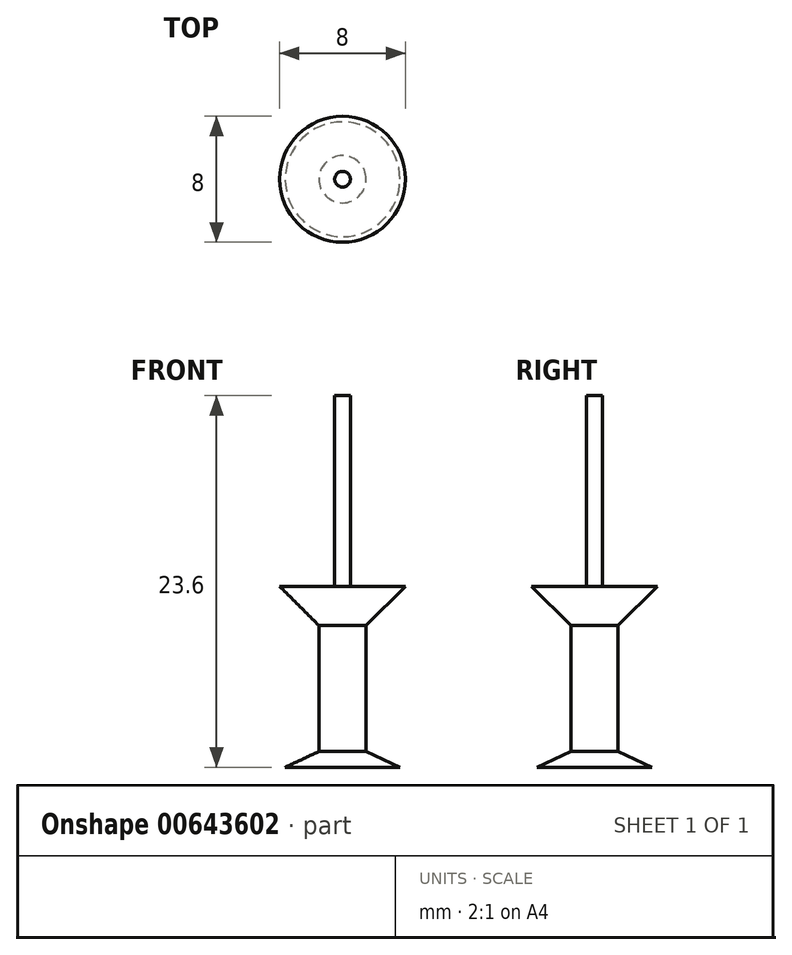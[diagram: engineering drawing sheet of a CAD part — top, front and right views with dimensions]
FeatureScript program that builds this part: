
annotation { "Feature Type Name" : "Feature", "Feature Type Description" : "" }
export const myFeature = defineFeature(function(context is Context, id is Id, definition is map)
    precondition{}
    {
        {
            var Q0;
            Q0=qCreatedBy(makeId("Right.planeOp"),FACE);
            var sketch = newSketch(context, id + "F0", { "sketchPlane" : qUnion([Q0])});
            skLineSegment(sketch, "E0", {"start": v(0, 0) * mm, "end": v(0.5, 0) * mm});
            skLineSegment(sketch, "E1", {"start": v(0.5, 0) * mm, "end": v(0, 0.87) * mm});
            skLineSegment(sketch, "E2", {"start": v(0, 0.87) * mm, "end": v(0, 0) * mm});
            skSolve(sketch);
        }
        {
            var Q0;
            Q0 = qSketchRegion(id + "F0", true);
            var Q1;
            Q1=sQuery(id+"F0.wireOp",EDGE,"E1");
            var Q2;
            Q2=sQuery(id+"F0.wireOp",EDGE,"E0");
            var Q3;
            Q3=sQuery(id+"F0.wireOp",EDGE,"E2");
            revolve(context, id + "F1", {"bodyType" : ToolBodyType.SURFACE, "entities" : qUnion([Q0]), "surfaceEntities" : qUnion([Q1, Q2]), "axis" : qUnion([Q3]), "revolveType" : RevolveType.FULL});
        }
        {
            var Q0;
            Q0=makeQuery(id+"F1.opRevolve","SWEPT_FACE",FACE,{"disambiguationData":[OSD([sQuery(id+"F0.wireOp",EDGE,"E0")])]});
            var sketch = newSketch(context, id + "F2", { "sketchPlane" : qUnion([Q0])});
            skSolve(sketch);
        }
        {
            var Q0;
            Q0=makeQuery(id+"F2.imprint","IMPRINT",FACE,{"disambiguationData":[TD([[makeQuery(id+"F2.imprint","IMPRINT",EDGE,{"derivedFrom":makeQuery(id+"F1.opRevolve","SWEPT_EDGE",EDGE,{"disambiguationData":[OSD([sQuery(id+"F0.wireOp",VERTEX,"E0.end")])]})}),1.0]])]});
            var Q1;
            Q1=makeQuery(id+"F1.opRevolve","SWEPT_FACE",FACE,{"disambiguationData":[OSD([sQuery(id+"F0.wireOp",EDGE,"E0")])]});
            extrude(context, id + "F3", {"entities" : qUnion([Q0, Q1]), "depth" : 12.1 * mm, "offsetDistance" : 25 * mm});
        }
        {
            var Q0;
            Q0=makeQuery(id+"F3.opExtrude","CAP_FACE",FACE,{"disambiguationData":[OSD([sQuery(id+"F0.wireOp",VERTEX,"E0.end")])],"isStart":false});
            var sketch = newSketch(context, id + "F4", { "sketchPlane" : qUnion([Q0])});
            skCircle(sketch, "E3", {"center": v(0, 0) * mm, "radius": 4 * mm});
            skSolve(sketch);
        }
        {
            var Q0;
            Q0 = qSketchRegion(id + "F4", true);
            extrude(context, id + "F5", {"entities" : qUnion([Q0]), "operationType" : NewBodyOperationType.ADD, "depth" : 2.5 * mm, "offsetDistance" : 25 * mm, "hasDraft" : true, "draftAngle" : 45 * degree, "draftPullDirection" : true});
        }
        {
            var Q0;
            Q0=makeQuery(id+"F5.opExtrude","CAP_FACE",FACE,{"disambiguationData":[OSD([sQuery(id+"F4.wireOp",EDGE,"E3")])],"isStart":false});
            var sketch = newSketch(context, id + "F6", { "sketchPlane" : qUnion([Q0])});
            skSolve(sketch);
        }
        {
            var Q0;
            Q0=makeQuery(id+"F6.imprint","IMPRINT",FACE,{"disambiguationData":[TD([[makeQuery(id+"F6.imprint","IMPRINT",EDGE,{"derivedFrom":makeQuery(id+"F5.opExtrude","CAP_EDGE",EDGE,{"disambiguationData":[OSD([sQuery(id+"F4.wireOp",EDGE,"E3")])],"isStart":false})}),1.0]])]});
            extrude(context, id + "F7", {"entities" : qUnion([Q0]), "operationType" : NewBodyOperationType.ADD, "depth" : 8 * mm, "offsetDistance" : 25 * mm});
        }
        {
            var Q0;
            Q0=makeQuery(id+"F7.opExtrude","CAP_FACE",FACE,{"disambiguationData":[OSD([sQuery(id+"F4.wireOp",EDGE,"E3")])],"isStart":false});
            var sketch = newSketch(context, id + "F8", { "sketchPlane" : qUnion([Q0])});
            skSolve(sketch);
        }
        {
            var Q0;
            Q0=makeQuery(id+"F8.imprint","IMPRINT",FACE,{"disambiguationData":[TD([[makeQuery(id+"F8.imprint","IMPRINT",EDGE,{"derivedFrom":makeQuery(id+"F7.opExtrude","CAP_EDGE",EDGE,{"disambiguationData":[OSD([sQuery(id+"F4.wireOp",EDGE,"E3")])],"isStart":false})}),1.0]])]});
            extrude(context, id + "F9", {"entities" : qUnion([Q0]), "operationType" : NewBodyOperationType.ADD, "depth" : 1 * mm, "offsetDistance" : 25 * mm, "hasDraft" : true, "draftAngle" : 65 * degree});
        }
    });
